# Revit family: Emergency_Equipment-Haws_Corporation-Eye_Face_Wash_7360B_7460B new
name_source: partatom
category: Plumbing Fixtures
revit_build: Autodesk Revit Architecture 2015 (Build: 20160512_1515(x64)
units: mm (PartAtom-declared; Revit-internal decimal feet)

## types (1)
- 7360B-7460B
    Assembly Code = D2010610
    Bowl = Metal - Haws Corporation - Green Powder Coating
    Bowl Diam. = 0' - 11"
    Bracket = Metal - Haws Corporation - Galvanized Steel
    CW Connection = Yes
    CWFU = 1
    Cost = 0 $
    Cost Note = For Cost information please visit the Resource tab in the Product Page URL
    Default Elevation = 2' - 11 3/4"
    Description = Eyewash streams provide zero vertical velocity stream engineering with even laminar flow for enhanced comfort
    Flow = 4 GPM
    HW Connection = No
    HWFU = 0
    Head Level = 3' - 4"
    Keynote = 15400
    Manufacturer = Haws Corporation
    Model = 7360B-7460B
    Product Documentation Link = https://www.hawsco.com
    Product Page URL = http://www.hawsco.com
    Sanitary Radius = 0' - 0 5/8"
    Series = AXION MSR™ Eye/Face Wash
    Supply Radius = 0' - 0 1/4"
    Tubing = Metal - Haws Corporation - Smokey Pearl
    Type Comments = Features a round 11" stainless steel receptor and aluminum wall bracket for long life
    URL = http://www.hawsco.com
    Vent Connection = No
    Version = 2014-v2.0a
    WFU = 1
    Waste Connection = Yes
    Waste Level = 0' - 10 3/8"

## geometry (parser evidence)
native form markers: Blend x12, Sweep x3
no freeform markers — native parametric forms only
